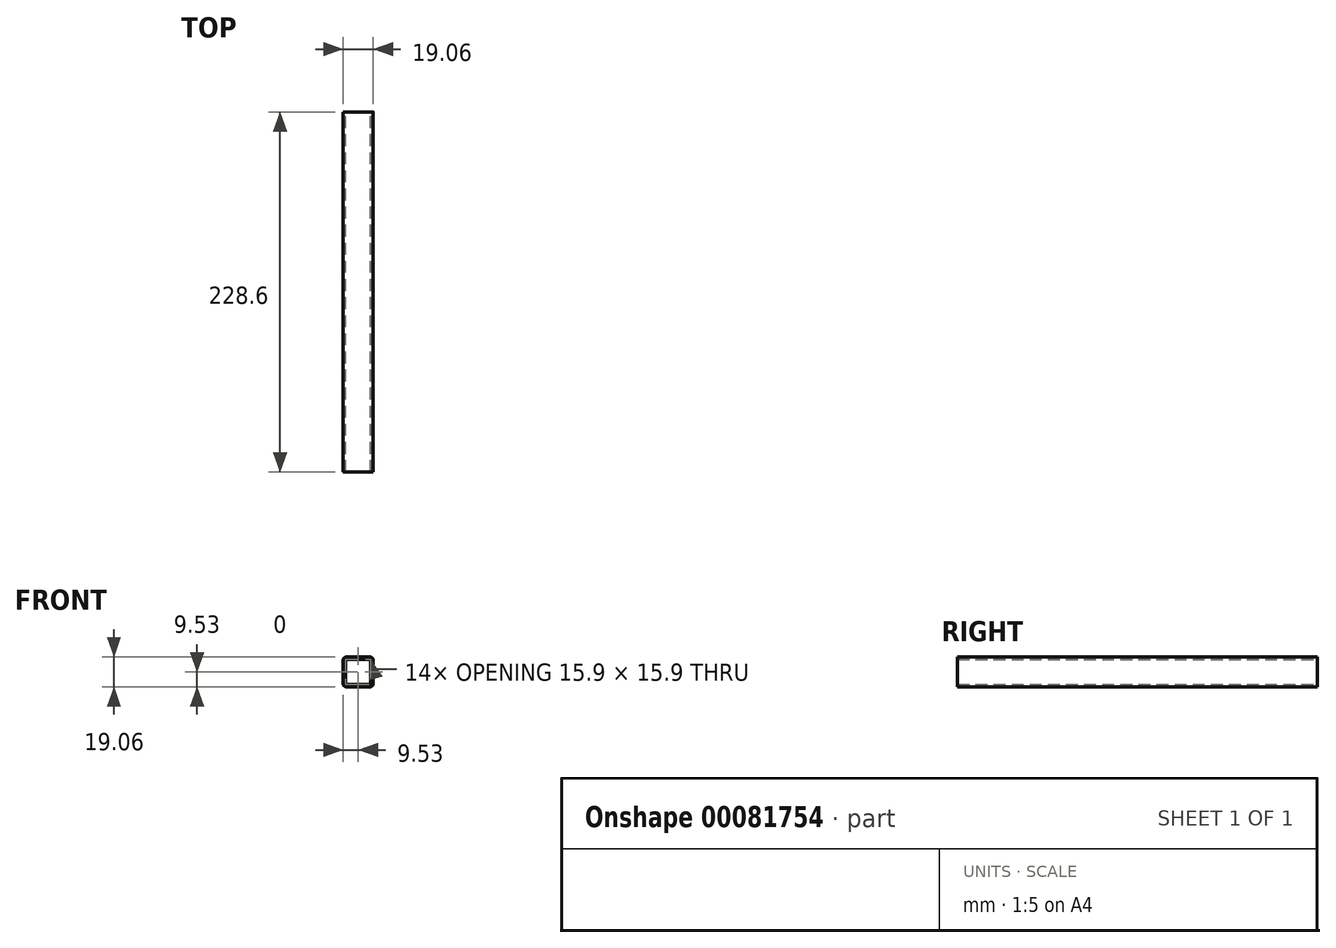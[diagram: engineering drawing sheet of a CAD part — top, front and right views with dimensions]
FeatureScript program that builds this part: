
annotation { "Feature Type Name" : "Feature", "Feature Type Description" : "" }
export const myFeature = defineFeature(function(context is Context, id is Id, definition is map)
    precondition{}
    {
        {
            var Q0;
            Q0=qCreatedBy(makeId("Front.planeOp"),FACE);
            var sketch = newSketch(context, id + "F0", { "sketchPlane" : qUnion([Q0])});
            skLineSegment(sketch, "E0.bottom", {"start": v(7.44, -9.52) * mm, "end": v(-7.44, -9.53) * mm});
            skLineSegment(sketch, "E0.top", {"start": v(7.44, 9.53) * mm, "end": v(-7.44, 9.52) * mm});
            skLineSegment(sketch, "E0.left", {"start": v(9.53, -7.44) * mm, "end": v(9.53, 7.44) * mm});
            skLineSegment(sketch, "E0.right", {"start": v(-9.53, -7.44) * mm, "end": v(-9.53, 7.44) * mm});
            skPoint(sketch, "E0.middle", {"position": v(0, 0) * mm});
            skLineSegment(sketch, "E1.bottom", {"start": v(7.44, -7.95) * mm, "end": v(-7.44, -7.95) * mm});
            skLineSegment(sketch, "E1.top", {"start": v(7.44, 7.95) * mm, "end": v(-7.44, 7.95) * mm});
            skLineSegment(sketch, "E1.left", {"start": v(7.95, -7.44) * mm, "end": v(7.95, 7.44) * mm});
            skLineSegment(sketch, "E1.right", {"start": v(-7.95, -7.44) * mm, "end": v(-7.95, 7.44) * mm});
            skPoint(sketch, "E2.visualSharp", {"position": v(-7.95, 7.95) * mm});
            skArc(sketch, "E2.filletArc", {"start": v(-7.44, 7.95) * mm, "mid": v(-7.8, 7.8) * mm, "end": v(-7.95, 7.44) * mm});
            skPoint(sketch, "E3.visualSharp", {"position": v(7.95, 7.95) * mm});
            skArc(sketch, "E3.filletArc", {"start": v(7.95, 7.44) * mm, "mid": v(7.8, 7.8) * mm, "end": v(7.44, 7.95) * mm});
            skPoint(sketch, "E4.visualSharp", {"position": v(7.95, -7.95) * mm});
            skArc(sketch, "E4.filletArc", {"start": v(7.44, -7.95) * mm, "mid": v(7.8, -7.8) * mm, "end": v(7.95, -7.44) * mm});
            skPoint(sketch, "E5.visualSharp", {"position": v(-7.95, -7.95) * mm});
            skArc(sketch, "E5.filletArc", {"start": v(-7.95, -7.44) * mm, "mid": v(-7.8, -7.8) * mm, "end": v(-7.44, -7.95) * mm});
            skPoint(sketch, "E6.visualSharp", {"position": v(9.53, 9.53) * mm});
            skArc(sketch, "E6.filletArc", {"start": v(9.53, 7.44) * mm, "mid": v(8.91, 8.91) * mm, "end": v(7.44, 9.53) * mm});
            skPoint(sketch, "E7.visualSharp", {"position": v(-9.53, 9.52) * mm});
            skArc(sketch, "E7.filletArc", {"start": v(-7.44, 9.53) * mm, "mid": v(-8.91, 8.91) * mm, "end": v(-9.53, 7.44) * mm});
            skPoint(sketch, "E8.visualSharp", {"position": v(-9.53, -9.53) * mm});
            skArc(sketch, "E8.filletArc", {"start": v(-9.53, -7.44) * mm, "mid": v(-8.91, -8.91) * mm, "end": v(-7.44, -9.52) * mm});
            skPoint(sketch, "E9.visualSharp", {"position": v(9.53, -9.52) * mm});
            skArc(sketch, "E9.filletArc", {"start": v(7.44, -9.52) * mm, "mid": v(8.91, -8.91) * mm, "end": v(9.52, -7.44) * mm});
            skSolve(sketch);
        }
        {
            var Q0;
            Q0=qSketchRegion(id+"F0",true);
            extrude(context, id + "F1", {"entities" : qUnion([Q0]), "depth" : 228.6 * mm});
        }
    });
